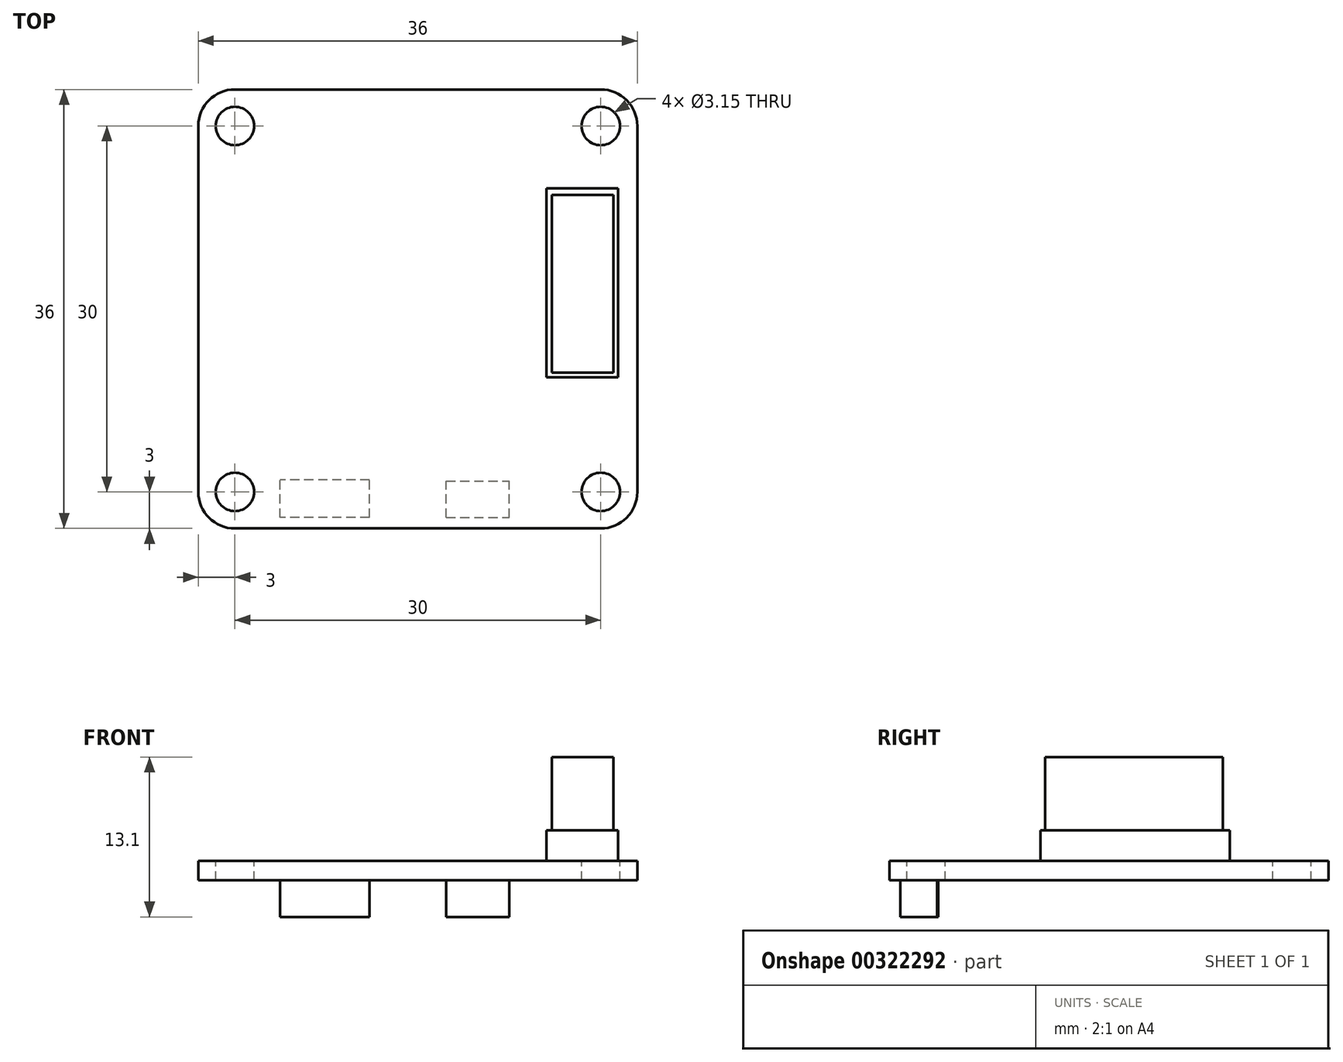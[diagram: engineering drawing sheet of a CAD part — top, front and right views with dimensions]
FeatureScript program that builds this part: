
annotation { "Feature Type Name" : "Feature", "Feature Type Description" : "" }
export const myFeature = defineFeature(function(context is Context, id is Id, definition is map)
    precondition{}
    {
        {
            var Q0;
            Q0=qCreatedBy(makeId("Top.planeOp"),FACE);
            var sketch = newSketch(context, id + "F0", { "sketchPlane" : qUnion([Q0])});
            skLineSegment(sketch, "E0.bottom", {"start": v(-18, 18) * mm, "end": v(18, 18) * mm});
            skLineSegment(sketch, "E0.top", {"start": v(-18, -18) * mm, "end": v(18, -18) * mm});
            skLineSegment(sketch, "E0.left", {"start": v(-18, 18) * mm, "end": v(-18, -18) * mm});
            skLineSegment(sketch, "E0.right", {"start": v(18, 18) * mm, "end": v(18, -18) * mm});
            skPoint(sketch, "E0.middle", {"position": v(0, 0) * mm});
            skLineSegment(sketch, "E1.bottom", {"start": v(-15, 15) * mm, "end": v(15, 15) * mm, "construction": true});
            skLineSegment(sketch, "E1.top", {"start": v(-15, -15) * mm, "end": v(15, -15) * mm, "construction": true});
            skLineSegment(sketch, "E1.left", {"start": v(-15, 15) * mm, "end": v(-15, -15) * mm, "construction": true});
            skLineSegment(sketch, "E1.right", {"start": v(15, 15) * mm, "end": v(15, -15) * mm, "construction": true});
            skSolve(sketch);
        }
        {
            var Q0;
            Q0=qSketchRegion(id+"F0",true);
            extrude(context, id + "F1", {"entities" : qUnion([Q0]), "oppositeDirection" : true, "depth" : 1.6 * mm});
        }
        {
            var Q0;
            Q0=makeQuery(id+"F1.opExtrude","SWEPT_EDGE",EDGE,{"disambiguationData":[OSD([sQuery(id+"F0.wireOp",EDGE,"E0.top"),sQuery(id+"F0.wireOp",EDGE,"E0.right")])]});
            var Q1;
            Q1=makeQuery(id+"F1.opExtrude","SWEPT_EDGE",EDGE,{"disambiguationData":[OSD([sQuery(id+"F0.wireOp",EDGE,"E0.top"),sQuery(id+"F0.wireOp",EDGE,"E0.left")])]});
            var Q2;
            Q2=makeQuery(id+"F1.opExtrude","SWEPT_EDGE",EDGE,{"disambiguationData":[OSD([sQuery(id+"F0.wireOp",EDGE,"E0.bottom"),sQuery(id+"F0.wireOp",EDGE,"E0.right")])]});
            var Q3;
            Q3=makeQuery(id+"F1.opExtrude","SWEPT_EDGE",EDGE,{"disambiguationData":[OSD([sQuery(id+"F0.wireOp",EDGE,"E0.bottom"),sQuery(id+"F0.wireOp",EDGE,"E0.left")])]});
            fillet(context, id + "F2", {"entities" : qUnion([Q0, Q1, Q2, Q3]), "radius" : 3 * mm, "tangentPropagation" : true, "allowEdgeOverflow" : false});
        }
        {
            var Q0;
            Q0=sQuery(id+"F0.wireOp",VERTEX,"E1.left.start");
            var Q1;
            Q1=sQuery(id+"F0.wireOp",VERTEX,"E1.bottom.end");
            var Q2;
            Q2=sQuery(id+"F0.wireOp",VERTEX,"E1.top.end");
            var Q3;
            Q3=sQuery(id+"F0.wireOp",VERTEX,"E1.top.start");
            var Q4;
            Q4=makeQuery(id+"F1.opExtrude","SWEPT_BODY",BODY,{"disambiguationData":[OSD([sQuery(id+"F0.wireOp",EDGE,"E0.bottom"),sQuery(id+"F0.wireOp",EDGE,"E0.top"),sQuery(id+"F0.wireOp",EDGE,"E0.left"),sQuery(id+"F0.wireOp",EDGE,"E0.right")])]});
            hole(context, id + "F3", {"style" : HoleStyle.SIMPLE, "endStyle" : HoleEndStyle.THROUGH, "standardTappedOrClearance" : lookupTablePath({ "standard" : "ISO", "fit" : "Close", "size" : "M3", "type" : "Clearance" }), "standardBlindInLast" : lookupTablePath({ "fit" : "Close", "standard" : "ISO", "size" : "M3", "type" : "Clearance" }), "holeDiameter" : 3.15 * mm, "tappedDepth" : 12.7 * mm, "tapClearance" : 3, "locations" : qUnion([Q0, Q1, Q2, Q3]), "scope" : qUnion([Q4])});
        }
        {
            var Q0;
            Q0=makeQuery(id+"F1.opExtrude","CAP_FACE",FACE,{"disambiguationData":[OSD([sQuery(id+"F0.wireOp",EDGE,"E0.bottom"),sQuery(id+"F0.wireOp",EDGE,"E0.top"),sQuery(id+"F0.wireOp",EDGE,"E0.left"),sQuery(id+"F0.wireOp",EDGE,"E0.right")])],"isStart":false});
            var sketch = newSketch(context, id + "F4", { "sketchPlane" : qUnion([Q0])});
            skLineSegment(sketch, "E2.bottom", {"start": v(2.33, 17.1) * mm, "end": v(7.5, 17.1) * mm});
            skLineSegment(sketch, "E2.top", {"start": v(2.33, 14.1) * mm, "end": v(7.5, 14.1) * mm});
            skLineSegment(sketch, "E2.left", {"start": v(2.33, 17.1) * mm, "end": v(2.33, 14.1) * mm});
            skLineSegment(sketch, "E2.right", {"start": v(7.5, 17.1) * mm, "end": v(7.5, 14.1) * mm});
            skLineSegment(sketch, "E3.bottom", {"start": v(-3.97, 17.1) * mm, "end": v(-11.3, 17.1) * mm});
            skLineSegment(sketch, "E3.top", {"start": v(-3.97, 14) * mm, "end": v(-11.3, 14) * mm});
            skLineSegment(sketch, "E3.left", {"start": v(-3.97, 17.1) * mm, "end": v(-3.97, 14) * mm});
            skLineSegment(sketch, "E3.right", {"start": v(-11.3, 17.1) * mm, "end": v(-11.3, 14) * mm});
            skSolve(sketch);
        }
        {
            var Q0;
            Q0=qSketchRegion(id+"F4",true);
            extrude(context, id + "F5", {"entities" : qUnion([Q0]), "operationType" : NewBodyOperationType.ADD, "depth" : 3 * mm});
        }
        {
            var Q0;
            Q0=makeQuery(id+"F0.imprint","IMPRINT",FACE,{"disambiguationData":[TD([[makeQuery(id+"F0.imprint","IMPRINT",EDGE,{"derivedFrom":sQuery(id+"F0.wireOp",EDGE,"E0.bottom")}),-1.0]])]});
            var sketch = newSketch(context, id + "F6", { "sketchPlane" : qUnion([Q0])});
            skLineSegment(sketch, "E4.bottom", {"start": v(16.42, 9.9) * mm, "end": v(10.55, 9.9) * mm});
            skLineSegment(sketch, "E4.top", {"start": v(16.42, -5.62) * mm, "end": v(10.55, -5.62) * mm});
            skLineSegment(sketch, "E4.left", {"start": v(16.42, 9.9) * mm, "end": v(16.42, -5.62) * mm});
            skLineSegment(sketch, "E4.right", {"start": v(10.55, 9.9) * mm, "end": v(10.55, -5.62) * mm});
            skSolve(sketch);
        }
        {
            var Q0;
            Q0=qSketchRegion(id+"F6",true);
            extrude(context, id + "F7", {"entities" : qUnion([Q0]), "operationType" : NewBodyOperationType.ADD, "depth" : 2.5 * mm});
        }
        {
            var Q0;
            Q0=makeQuery(id+"F7.opExtrude","CAP_FACE",FACE,{"disambiguationData":[OSD([sQuery(id+"F6.wireOp",EDGE,"E4.bottom"),sQuery(id+"F6.wireOp",EDGE,"E4.top"),sQuery(id+"F6.wireOp",EDGE,"E4.left"),sQuery(id+"F6.wireOp",EDGE,"E4.right")])],"isStart":false});
            var sketch = newSketch(context, id + "F8", { "sketchPlane" : qUnion([Q0])});
            skLineSegment(sketch, "E5.bottom", {"start": v(11, 9.35) * mm, "end": v(16.04, 9.35) * mm});
            skLineSegment(sketch, "E5.top", {"start": v(11, -5.23) * mm, "end": v(16.04, -5.23) * mm});
            skLineSegment(sketch, "E5.left", {"start": v(11, 9.35) * mm, "end": v(11, -5.23) * mm});
            skLineSegment(sketch, "E5.right", {"start": v(16.04, 9.35) * mm, "end": v(16.04, -5.23) * mm});
            skSolve(sketch);
        }
        {
            var Q0;
            Q0=makeQuery(id+"F8.imprint","IMPRINT",FACE,{"disambiguationData":[TD([[makeQuery(id+"F8.imprint","IMPRINT",EDGE,{"derivedFrom":sQuery(id+"F8.wireOp",EDGE,"E5.bottom")}),-1.0]])]});
            extrude(context, id + "F9", {"entities" : qUnion([Q0]), "operationType" : NewBodyOperationType.ADD, "depth" : 6 * mm});
        }
    });
